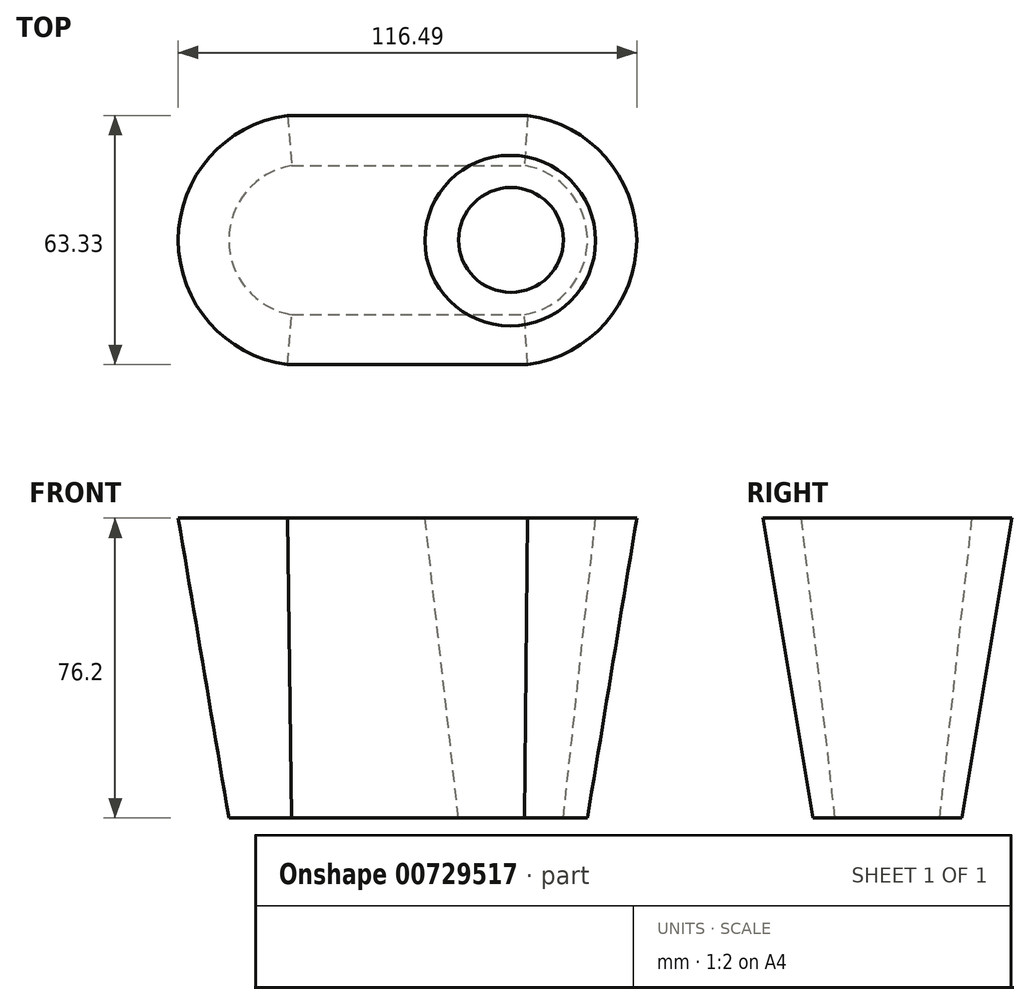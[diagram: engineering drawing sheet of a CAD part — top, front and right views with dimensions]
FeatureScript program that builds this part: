
annotation { "Feature Type Name" : "Feature", "Feature Type Description" : "" }
export const myFeature = defineFeature(function(context is Context, id is Id, definition is map)
    precondition{}
    {
        {
            var Q0;
            Q0=qCreatedBy(makeId("Top.planeOp"),FACE);
            var sketch = newSketch(context, id + "F0", { "sketchPlane" : qUnion([Q0])});
            skLineSegment(sketch, "E0.0", {"start": v(-39.12, -6.35) * mm, "end": v(20, -6.35) * mm});
            skArc(sketch, "E0.1", {"start": v(-39.12, 31.58) * mm, "mid": v(-55.1, 12.61) * mm, "end": v(-39.12, -6.35) * mm});
            skLineSegment(sketch, "E0.2", {"start": v(-39.12, 31.58) * mm, "end": v(20, 31.58) * mm});
            skArc(sketch, "E0.3", {"start": v(20, -6.35) * mm, "mid": v(35.99, 12.61) * mm, "end": v(20, 31.58) * mm});
            skSolve(sketch);
        }
        {
            var Q0;
            {var subQ1=sQuery(id+"F0.wireOp",EDGE,"StqDSTxA-OND6-a5W0-wKk5-HIJeRuu1olZO");Q0=makeQuery(id+"F0.imprint","IMPRINT",FACE,{"disambiguationData":[TD([[makeQuery(id+"F0.imprint","IMPRINT",EDGE,{"derivedFrom":subQ1}),-1.0]])]});}
            var Q1;
            Q1=qCreatedBy(makeId("Top.planeOp"),FACE);
            cPlane(context, id + "F1", {"entities" : qUnion([Q0, Q1]), "cplaneType" : CPlaneType.OFFSET, "offset" : 76.2 * mm, "width" : 152.4 * mm, "height" : 152.4 * mm});
        }
        {
            var Q0;
            Q0=qCreatedBy(id+"F1.planeOp",FACE);
            var sketch = newSketch(context, id + "F2", { "sketchPlane" : qUnion([Q0])});
            skArc(sketch, "E1.0", {"start": v(-40.23, 44.28) * mm, "mid": v(-67.97, 12.61) * mm, "end": v(-40.23, -19.05) * mm});
            skLineSegment(sketch, "E1.1", {"start": v(-40.23, 44.28) * mm, "end": v(20.78, 44.28) * mm});
            skArc(sketch, "E1.2", {"start": v(20.78, -19.05) * mm, "mid": v(48.52, 12.61) * mm, "end": v(20.78, 44.28) * mm});
            skLineSegment(sketch, "E1.3", {"start": v(-40.23, -19.05) * mm, "end": v(20.78, -19.05) * mm});
            skSolve(sketch);
        }
        {
            var Q0;
            Q0=makeQuery(id+"F2.imprint","IMPRINT",FACE,{"disambiguationData":[TD([[makeQuery(id+"F2.imprint","IMPRINT",EDGE,{"derivedFrom":sQuery(id+"F2.wireOp",EDGE,"E1.0")}),1.0]])]});
            var Q1;
            Q1=makeQuery(id+"F0.imprint","IMPRINT",FACE,{"disambiguationData":[TD([[makeQuery(id+"F0.imprint","IMPRINT",EDGE,{"derivedFrom":sQuery(id+"F0.wireOp",EDGE,"E0.0")}),1.0]])]});
            loft(context, id + "F3", {"sheetProfilesArray" : [{ "sheetProfileEntities" : qUnion([Q0]) }, { "sheetProfileEntities" : qUnion([Q1]) }]});
        }
        {
            var Q0;
            Q0=qCreatedBy(id+"F1.planeOp",FACE);
            var sketch = newSketch(context, id + "F4", { "sketchPlane" : qUnion([Q0])});
            skCircle(sketch, "E2", {"center": v(16.39, 12.46) * mm, "radius": 21.68 * mm});
            skSolve(sketch);
        }
        {
            var Q0;
            Q0=qCreatedBy(makeId("Top.planeOp"),FACE);
            var sketch = newSketch(context, id + "F5", { "sketchPlane" : qUnion([Q0])});
            skCircle(sketch, "E3", {"center": v(16.56, 12.64) * mm, "radius": 13.31 * mm});
            skSolve(sketch);
        }
        {
            var Q1;
            Q1=makeQuery(id+"F4.imprint","IMPRINT",FACE,{"disambiguationData":[TD([[makeQuery(id+"F4.imprint","IMPRINT",EDGE,{"derivedFrom":sQuery(id+"F4.wireOp",EDGE,"E2")}),1.0]])]});
            var Q2;
            Q2=makeQuery(id+"F5.imprint","IMPRINT",FACE,{"disambiguationData":[TD([[makeQuery(id+"F5.imprint","IMPRINT",EDGE,{"derivedFrom":sQuery(id+"F5.wireOp",EDGE,"E3")}),1.0]])]});
            loft(context, id + "F6", {"operationType" : NewBodyOperationType.REMOVE, "sheetProfilesArray" : [{ "sheetProfileEntities" : qUnion([Q1]) }, { "sheetProfileEntities" : qUnion([Q2]) }]});
        }
    });
